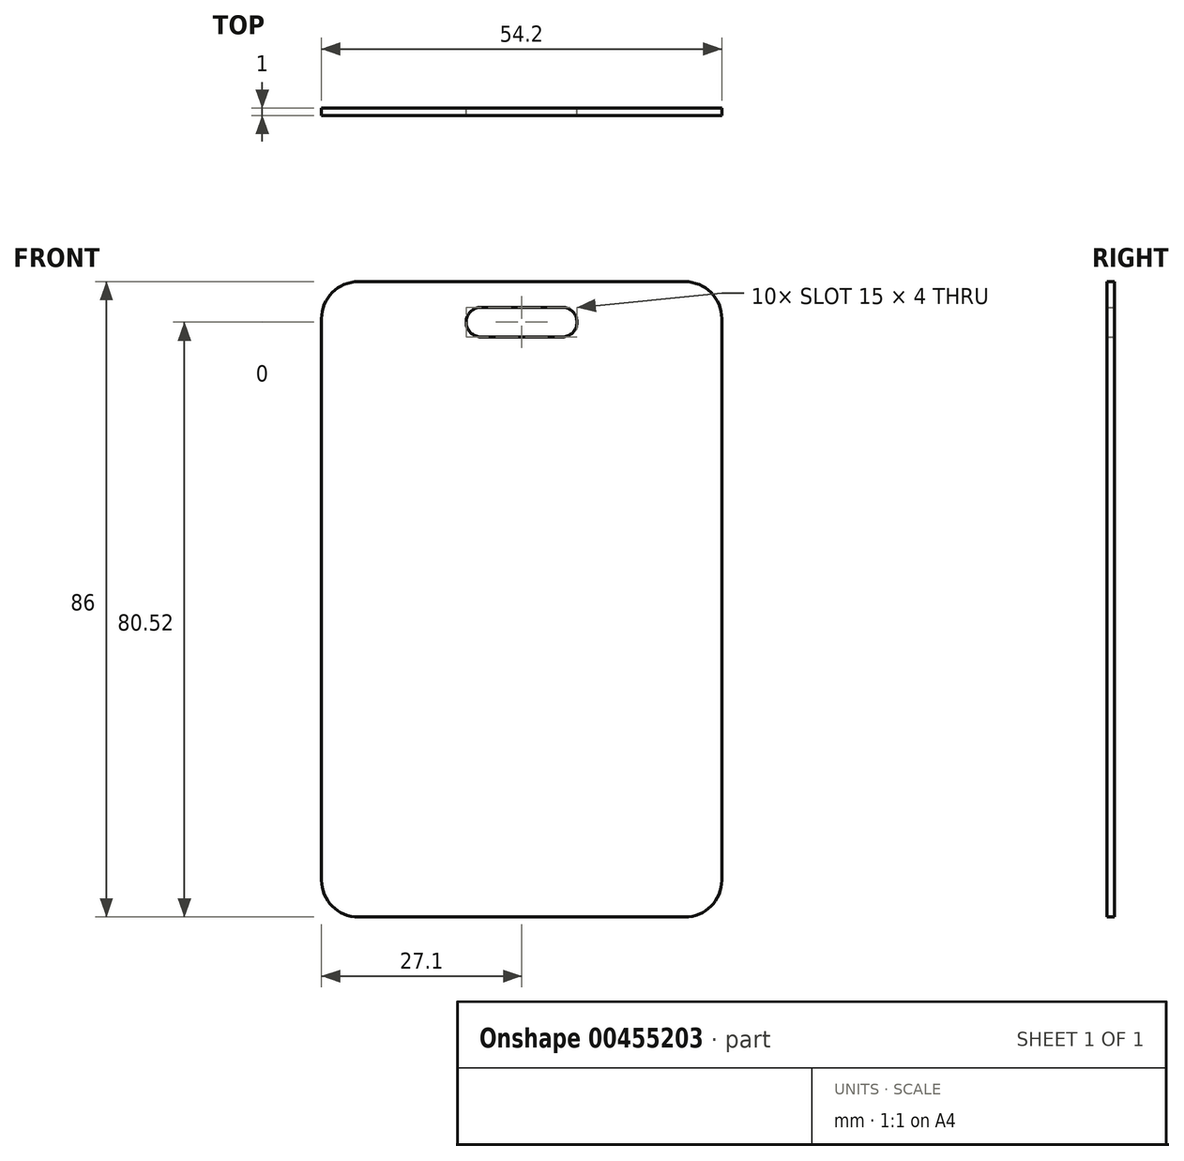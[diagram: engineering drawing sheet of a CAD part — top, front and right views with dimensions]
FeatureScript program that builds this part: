
annotation { "Feature Type Name" : "Feature", "Feature Type Description" : "" }
export const myFeature = defineFeature(function(context is Context, id is Id, definition is map)
    precondition{}
    {
        {
            var Q0;
            Q0=qCreatedBy(makeId("Front.planeOp"),FACE);
            var sketch = newSketch(context, id + "F0", { "sketchPlane" : qUnion([Q0])});
            skLineSegment(sketch, "E0.bottom", {"start": v(-27.1, 43) * mm, "end": v(27.1, 43) * mm});
            skLineSegment(sketch, "E0.top", {"start": v(-27.1, -43) * mm, "end": v(27.1, -43) * mm});
            skLineSegment(sketch, "E0.left", {"start": v(-27.1, 43) * mm, "end": v(-27.1, -43) * mm});
            skLineSegment(sketch, "E0.right", {"start": v(27.1, 43) * mm, "end": v(27.1, -43) * mm});
            skLineSegment(sketch, "E1.bottom", {"start": v(-7.5, 39.52) * mm, "end": v(7.5, 39.52) * mm});
            skLineSegment(sketch, "E1.top", {"start": v(-7.5, 35.52) * mm, "end": v(7.5, 35.52) * mm});
            skLineSegment(sketch, "E1.left", {"start": v(-7.5, 39.52) * mm, "end": v(-7.5, 35.52) * mm});
            skLineSegment(sketch, "E1.right", {"start": v(7.5, 39.52) * mm, "end": v(7.5, 35.52) * mm});
            skLineSegment(sketch, "E2", {"start": v(-7.5, 37.52) * mm, "end": v(7.5, 37.52) * mm});
            skSolve(sketch);
        }
        {
            var Q0;
            Q0=makeQuery(id+"F0.imprint","IMPRINT",FACE,{"disambiguationData":[TD([[makeQuery(id+"F0.imprint","IMPRINT",EDGE,{"derivedFrom":sQuery(id+"F0.wireOp",EDGE,"E0.bottom")}),-1.0]])]});
            extrude(context, id + "F1", {"entities" : qUnion([Q0]), "depth" : 1 * mm});
        }
        {
            var Q0;
            Q0=makeQuery(id+"F1.opExtrude","SWEPT_EDGE",EDGE,{"disambiguationData":[OSD([sQuery(id+"F0.wireOp",EDGE,"E0.bottom"),sQuery(id+"F0.wireOp",EDGE,"E0.left")])]});
            var Q1;
            Q1=makeQuery(id+"F1.opExtrude","SWEPT_EDGE",EDGE,{"disambiguationData":[OSD([sQuery(id+"F0.wireOp",EDGE,"E0.bottom"),sQuery(id+"F0.wireOp",EDGE,"E0.right")])]});
            var Q2;
            Q2=makeQuery(id+"F1.opExtrude","SWEPT_EDGE",EDGE,{"disambiguationData":[OSD([sQuery(id+"F0.wireOp",EDGE,"E0.top"),sQuery(id+"F0.wireOp",EDGE,"E0.right")])]});
            var Q3;
            Q3=makeQuery(id+"F1.opExtrude","SWEPT_EDGE",EDGE,{"disambiguationData":[OSD([sQuery(id+"F0.wireOp",EDGE,"E0.top"),sQuery(id+"F0.wireOp",EDGE,"E0.left")])]});
            fillet(context, id + "F2", {"entities" : qUnion([Q0, Q1, Q2, Q3]), "radius" : 5 * mm, "tangentPropagation" : true, "allowEdgeOverflow" : false});
        }
        {
            var Q0;
            Q0=makeQuery(id+"F1.opExtrude","SWEPT_EDGE",EDGE,{"disambiguationData":[OSD([sQuery(id+"F0.wireOp",EDGE,"E1.bottom"),sQuery(id+"F0.wireOp",EDGE,"E1.left")])]});
            var Q1;
            Q1=makeQuery(id+"F1.opExtrude","SWEPT_EDGE",EDGE,{"disambiguationData":[OSD([sQuery(id+"F0.wireOp",EDGE,"E1.top"),sQuery(id+"F0.wireOp",EDGE,"E1.left")])]});
            var Q2;
            Q2=makeQuery(id+"F1.opExtrude","SWEPT_EDGE",EDGE,{"disambiguationData":[OSD([sQuery(id+"F0.wireOp",EDGE,"E1.top"),sQuery(id+"F0.wireOp",EDGE,"E1.right")])]});
            var Q3;
            Q3=makeQuery(id+"F1.opExtrude","SWEPT_EDGE",EDGE,{"disambiguationData":[OSD([sQuery(id+"F0.wireOp",EDGE,"E1.bottom"),sQuery(id+"F0.wireOp",EDGE,"E1.right")])]});
            fillet(context, id + "F3", {"entities" : qUnion([Q0, Q1, Q2, Q3]), "radius" : 2 * mm, "tangentPropagation" : true, "allowEdgeOverflow" : false});
        }
    });
